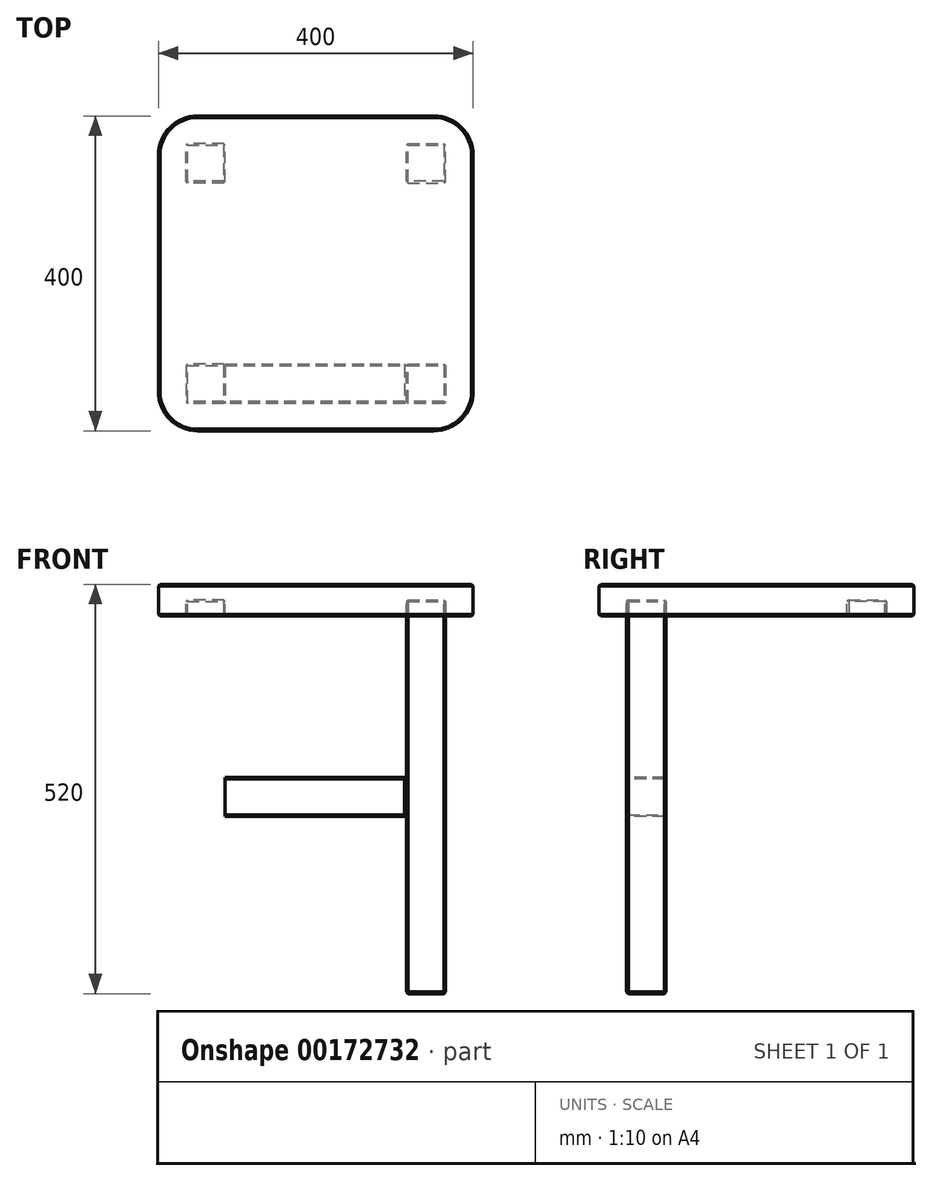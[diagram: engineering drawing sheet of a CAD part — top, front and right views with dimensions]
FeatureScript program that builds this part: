
annotation { "Feature Type Name" : "Feature", "Feature Type Description" : "" }
export const myFeature = defineFeature(function(context is Context, id is Id, definition is map)
    precondition{}
    {
        {
            var Q0;
            Q0=qCreatedBy(makeId("Top.planeOp"),FACE);
            var sketch = newSketch(context, id + "F0", { "sketchPlane" : qUnion([Q0])});
            skLineSegment(sketch, "E0.bottom", {"start": v(-200, -200) * mm, "end": v(200, -200) * mm});
            skLineSegment(sketch, "E0.top", {"start": v(-200, 200) * mm, "end": v(200, 200) * mm});
            skLineSegment(sketch, "E0.left", {"start": v(-200, -200) * mm, "end": v(-200, 200) * mm});
            skLineSegment(sketch, "E0.right", {"start": v(200, -200) * mm, "end": v(200, 200) * mm});
            skPoint(sketch, "E0.middle", {"position": v(0, 0) * mm});
            skSolve(sketch);
        }
        {
            var Q0;
            Q0=makeQuery(id+"F0.imprint","IMPRINT",FACE,{"disambiguationData":[TD([[makeQuery(id+"F0.imprint","IMPRINT",EDGE,{"derivedFrom":sQuery(id+"F0.wireOp",EDGE,"E0.bottom")}),1.0]])]});
            extrude(context, id + "F1", {"entities" : qUnion([Q0]), "depth" : 40 * mm});
        }
        {
            var Q0;
            Q0=makeQuery(id+"F1.opExtrude","CAP_FACE",FACE,{"disambiguationData":[OSD([sQuery(id+"F0.wireOp",EDGE,"E0.bottom"),sQuery(id+"F0.wireOp",EDGE,"E0.top"),sQuery(id+"F0.wireOp",EDGE,"E0.left"),sQuery(id+"F0.wireOp",EDGE,"E0.right")])],"isStart":true});
            var sketch = newSketch(context, id + "F2", { "sketchPlane" : qUnion([Q0])});
            skLineSegment(sketch, "E1.bottom", {"start": v(115, 115) * mm, "end": v(165, 115) * mm});
            skLineSegment(sketch, "E1.top", {"start": v(115, 165) * mm, "end": v(165, 165) * mm});
            skLineSegment(sketch, "E1.left", {"start": v(115, 115) * mm, "end": v(115, 165) * mm});
            skLineSegment(sketch, "E1.right", {"start": v(165, 115) * mm, "end": v(165, 165) * mm});
            skPoint(sketch, "E1.middle", {"position": v(140, 140) * mm});
            skLineSegment(sketch, "E2", {"start": v(140, 140) * mm, "end": v(200, 140) * mm, "construction": true});
            skLineSegment(sketch, "E3", {"start": v(140, 140) * mm, "end": v(140, 200) * mm, "construction": true});
            skLineSegment(sketch, "E4.MirrorCS", {"start": v(115, -115) * mm, "end": v(165, -115) * mm});
            skPoint(sketch, "E5.MirrorP", {"position": v(140, -140) * mm});
            skLineSegment(sketch, "E6.MirrorCS", {"start": v(165, -115) * mm, "end": v(165, -165) * mm});
            skLineSegment(sketch, "E7.MirrorCS", {"start": v(115, -165) * mm, "end": v(165, -165) * mm});
            skLineSegment(sketch, "E8.MirrorCS", {"start": v(115, -115) * mm, "end": v(115, -165) * mm});
            skPoint(sketch, "E9.MirrorP", {"position": v(-140, -140) * mm});
            skLineSegment(sketch, "E10.MirrorCS", {"start": v(-165, -115) * mm, "end": v(-165, -165) * mm});
            skLineSegment(sketch, "E11.MirrorCS", {"start": v(-115, -165) * mm, "end": v(-165, -165) * mm});
            skLineSegment(sketch, "E12.MirrorCS", {"start": v(-115, -115) * mm, "end": v(-165, -115) * mm});
            skLineSegment(sketch, "E13.MirrorCS", {"start": v(-115, -115) * mm, "end": v(-115, -165) * mm});
            skLineSegment(sketch, "E14.MirrorCS", {"start": v(-165, 115) * mm, "end": v(-165, 165) * mm});
            skLineSegment(sketch, "E15.MirrorCS", {"start": v(-115, 115) * mm, "end": v(-115, 165) * mm});
            skPoint(sketch, "E16.MirrorP", {"position": v(-140, 140) * mm});
            skLineSegment(sketch, "E17.MirrorCS", {"start": v(-115, 115) * mm, "end": v(-165, 115) * mm});
            skLineSegment(sketch, "E18.MirrorCS", {"start": v(-115, 165) * mm, "end": v(-165, 165) * mm});
            skSolve(sketch);
        }
        {
            var Q0;
            Q0 = qSketchRegion(id + "F2", true);
            extrude(context, id + "F3", {"entities" : qUnion([Q0]), "operationType" : NewBodyOperationType.REMOVE, "oppositeDirection" : true, "depth" : 20 * mm});
        }
        {
            var Q0;
            Q0=makeQuery(id+"F1.opExtrude","SWEPT_EDGE",EDGE,{"disambiguationData":[OSD([sQuery(id+"F0.wireOp",EDGE,"E0.bottom"),sQuery(id+"F0.wireOp",EDGE,"E0.right")])]});
            var Q1;
            Q1=makeQuery(id+"F1.opExtrude","SWEPT_EDGE",EDGE,{"disambiguationData":[OSD([sQuery(id+"F0.wireOp",EDGE,"E0.top"),sQuery(id+"F0.wireOp",EDGE,"E0.right")])]});
            var Q2;
            Q2=makeQuery(id+"F1.opExtrude","SWEPT_EDGE",EDGE,{"disambiguationData":[OSD([sQuery(id+"F0.wireOp",EDGE,"E0.top"),sQuery(id+"F0.wireOp",EDGE,"E0.left")])]});
            var Q3;
            Q3=makeQuery(id+"F1.opExtrude","SWEPT_EDGE",EDGE,{"disambiguationData":[OSD([sQuery(id+"F0.wireOp",EDGE,"E0.bottom"),sQuery(id+"F0.wireOp",EDGE,"E0.left")])]});
            fillet(context, id + "F4", {"entities" : qUnion([Q0, Q1, Q2, Q3]), "radius" : 50 * mm, "tangentPropagation" : true, "allowEdgeOverflow" : false});
        }
        {
            var Q0;
            Q0=makeQuery(id+"F3.boolean.opBoolean","COPY",FACE,{"derivedFrom":makeQuery(id+"F3.opExtrude","CAP_FACE",FACE,{"disambiguationData":[OSD([sQuery(id+"F2.wireOp",EDGE,"E1.bottom"),sQuery(id+"F2.wireOp",EDGE,"E1.top"),sQuery(id+"F2.wireOp",EDGE,"E1.left"),sQuery(id+"F2.wireOp",EDGE,"E1.right")])],"isStart":false})});
            extrude(context, id + "F5", {"entities" : qUnion([Q0]), "depth" : 500 * mm});
        }
        {
            var Q0;
            Q0=makeQuery(id+"F5.opExtrude","SWEPT_FACE",FACE,{"disambiguationData":[OSD([sQuery(id+"F2.wireOp",EDGE,"E1.left")])]});
            var sketch = newSketch(context, id + "F6", { "sketchPlane" : qUnion([Q0])});
            skLineSegment(sketch, "E19.bottom", {"start": v(165, -205) * mm, "end": v(115, -205) * mm});
            skLineSegment(sketch, "E19.top", {"start": v(165, -255) * mm, "end": v(115, -255) * mm});
            skLineSegment(sketch, "E19.left", {"start": v(165, -205) * mm, "end": v(165, -255) * mm});
            skLineSegment(sketch, "E19.right", {"start": v(115, -205) * mm, "end": v(115, -255) * mm});
            skSolve(sketch);
        }
        {
            var Q0;
            Q0 = qSketchRegion(id + "F6", true);
            var Q1;
            Q1=makeQuery(id+"F3.boolean.opBoolean","COPY",FACE,{"derivedFrom":makeQuery(id+"F3.opExtrude","SWEPT_FACE",FACE,{"disambiguationData":[OSD([sQuery(id+"F2.wireOp",EDGE,"E15.MirrorCS")])]})});
            extrude(context, id + "F7", {"entities" : qUnion([Q0]), "endBound" : BoundingType.UP_TO_SURFACE, "endBoundEntityFace" : qUnion([Q1]), "depth" : 25 * mm});
        }
        {
            var Q0;
            {var subQ0=sQuery(id+"F0.wireOp",EDGE,"E0.left");var subQ1=sQuery(id+"F0.wireOp",EDGE,"E0.bottom");Q0=makeQuery(id+"F4.opFillet","BLEND_EDGE",EDGE,{"blendedFrom":[makeQuery(id+"F1.opExtrude","SWEPT_EDGE",EDGE,{"disambiguationData":[OSD([subQ1,subQ0])]}),makeQuery(id+"F1.opExtrude","CAP_FACE",FACE,{"disambiguationData":[OSD([subQ1,sQuery(id+"F0.wireOp",EDGE,"E0.top"),subQ0,sQuery(id+"F0.wireOp",EDGE,"E0.right")])],"isStart":true})],"blendedInto":[makeQuery(id+"F1.opExtrude","CAP_FACE",FACE,{"disambiguationData":[OSD([subQ1,sQuery(id+"F0.wireOp",EDGE,"E0.top"),subQ0,sQuery(id+"F0.wireOp",EDGE,"E0.right")])],"isStart":true})]});}
            var Q1;
            {var subQ0=sQuery(id+"F0.wireOp",EDGE,"E0.right");var subQ1=sQuery(id+"F0.wireOp",EDGE,"E0.bottom");Q1=makeQuery(id+"F4.opFillet","BLEND_EDGE",EDGE,{"blendedFrom":[makeQuery(id+"F1.opExtrude","SWEPT_EDGE",EDGE,{"disambiguationData":[OSD([subQ1,subQ0])]}),makeQuery(id+"F1.opExtrude","CAP_FACE",FACE,{"disambiguationData":[OSD([subQ1,sQuery(id+"F0.wireOp",EDGE,"E0.top"),sQuery(id+"F0.wireOp",EDGE,"E0.left"),subQ0])],"isStart":false})],"blendedInto":[makeQuery(id+"F1.opExtrude","CAP_FACE",FACE,{"disambiguationData":[OSD([subQ1,sQuery(id+"F0.wireOp",EDGE,"E0.top"),sQuery(id+"F0.wireOp",EDGE,"E0.left"),subQ0])],"isStart":false})]});}
            var Q2;
            {var subQ0=sQuery(id+"F0.wireOp",EDGE,"E0.left");var subQ1=sQuery(id+"F0.wireOp",EDGE,"E0.top");Q2=makeQuery(id+"F4.opFillet","BLEND_EDGE",EDGE,{"blendedFrom":[makeQuery(id+"F1.opExtrude","SWEPT_EDGE",EDGE,{"disambiguationData":[OSD([subQ1,subQ0])]}),makeQuery(id+"F1.opExtrude","CAP_FACE",FACE,{"disambiguationData":[OSD([sQuery(id+"F0.wireOp",EDGE,"E0.bottom"),subQ1,subQ0,sQuery(id+"F0.wireOp",EDGE,"E0.right")])],"isStart":false})],"blendedInto":[makeQuery(id+"F1.opExtrude","CAP_FACE",FACE,{"disambiguationData":[OSD([sQuery(id+"F0.wireOp",EDGE,"E0.bottom"),subQ1,subQ0,sQuery(id+"F0.wireOp",EDGE,"E0.right")])],"isStart":false})]});}
            var Q3;
            {var subQ0=sQuery(id+"F0.wireOp",EDGE,"E0.left");var subQ1=sQuery(id+"F0.wireOp",EDGE,"E0.top");Q3=makeQuery(id+"F4.opFillet","BLEND_EDGE",EDGE,{"blendedFrom":[makeQuery(id+"F1.opExtrude","SWEPT_EDGE",EDGE,{"disambiguationData":[OSD([subQ1,subQ0])]}),makeQuery(id+"F1.opExtrude","CAP_FACE",FACE,{"disambiguationData":[OSD([sQuery(id+"F0.wireOp",EDGE,"E0.bottom"),subQ1,subQ0,sQuery(id+"F0.wireOp",EDGE,"E0.right")])],"isStart":true})],"blendedInto":[makeQuery(id+"F1.opExtrude","CAP_FACE",FACE,{"disambiguationData":[OSD([sQuery(id+"F0.wireOp",EDGE,"E0.bottom"),subQ1,subQ0,sQuery(id+"F0.wireOp",EDGE,"E0.right")])],"isStart":true})]});}
            var Q4;
            Q4=makeQuery(id+"F1.opExtrude","CAP_EDGE",EDGE,{"disambiguationData":[OSD([sQuery(id+"F0.wireOp",EDGE,"E0.bottom")])],"isStart":true});
            var Q5;
            Q5=makeQuery(id+"F1.opExtrude","CAP_EDGE",EDGE,{"disambiguationData":[OSD([sQuery(id+"F0.wireOp",EDGE,"E0.bottom")])],"isStart":false});
            var Q6;
            Q6=makeQuery(id+"F1.opExtrude","CAP_EDGE",EDGE,{"disambiguationData":[OSD([sQuery(id+"F0.wireOp",EDGE,"E0.left")])],"isStart":true});
            var Q7;
            Q7=makeQuery(id+"F1.opExtrude","CAP_EDGE",EDGE,{"disambiguationData":[OSD([sQuery(id+"F0.wireOp",EDGE,"E0.top")])],"isStart":false});
            var Q8;
            {var subQ0=sQuery(id+"F0.wireOp",EDGE,"E0.left");var subQ1=sQuery(id+"F0.wireOp",EDGE,"E0.bottom");Q8=makeQuery(id+"F4.opFillet","BLEND_EDGE",EDGE,{"blendedFrom":[makeQuery(id+"F1.opExtrude","SWEPT_EDGE",EDGE,{"disambiguationData":[OSD([subQ1,subQ0])]}),makeQuery(id+"F1.opExtrude","CAP_FACE",FACE,{"disambiguationData":[OSD([subQ1,sQuery(id+"F0.wireOp",EDGE,"E0.top"),subQ0,sQuery(id+"F0.wireOp",EDGE,"E0.right")])],"isStart":false})],"blendedInto":[makeQuery(id+"F1.opExtrude","CAP_FACE",FACE,{"disambiguationData":[OSD([subQ1,sQuery(id+"F0.wireOp",EDGE,"E0.top"),subQ0,sQuery(id+"F0.wireOp",EDGE,"E0.right")])],"isStart":false})]});}
            var Q9;
            Q9=makeQuery(id+"F1.opExtrude","CAP_EDGE",EDGE,{"disambiguationData":[OSD([sQuery(id+"F0.wireOp",EDGE,"E0.left")])],"isStart":false});
            var Q10;
            Q10=makeQuery(id+"F1.opExtrude","CAP_EDGE",EDGE,{"disambiguationData":[OSD([sQuery(id+"F0.wireOp",EDGE,"E0.right")])],"isStart":false});
            var Q11;
            {var subQ0=sQuery(id+"F0.wireOp",EDGE,"E0.right");var subQ1=sQuery(id+"F0.wireOp",EDGE,"E0.top");Q11=makeQuery(id+"F4.opFillet","BLEND_EDGE",EDGE,{"blendedFrom":[makeQuery(id+"F1.opExtrude","SWEPT_EDGE",EDGE,{"disambiguationData":[OSD([subQ1,subQ0])]}),makeQuery(id+"F1.opExtrude","CAP_FACE",FACE,{"disambiguationData":[OSD([sQuery(id+"F0.wireOp",EDGE,"E0.bottom"),subQ1,sQuery(id+"F0.wireOp",EDGE,"E0.left"),subQ0])],"isStart":false})],"blendedInto":[makeQuery(id+"F1.opExtrude","CAP_FACE",FACE,{"disambiguationData":[OSD([sQuery(id+"F0.wireOp",EDGE,"E0.bottom"),subQ1,sQuery(id+"F0.wireOp",EDGE,"E0.left"),subQ0])],"isStart":false})]});}
            var Q12;
            Q12=makeQuery(id+"F7.opExtrude","SWEPT_EDGE",EDGE,{"disambiguationData":[OSD([sQuery(id+"F2.wireOp",EDGE,"E1.top"),sQuery(id+"F2.wireOp",EDGE,"E1.left"),sQuery(id+"F6.wireOp",EDGE,"E19.bottom"),sQuery(id+"F6.wireOp",EDGE,"E19.left")])]});
            var Q13;
            Q13=makeQuery(id+"F7.opExtrude","SWEPT_EDGE",EDGE,{"disambiguationData":[OSD([sQuery(id+"F2.wireOp",EDGE,"E1.bottom"),sQuery(id+"F2.wireOp",EDGE,"E1.left"),sQuery(id+"F6.wireOp",EDGE,"E19.bottom"),sQuery(id+"F6.wireOp",EDGE,"E19.right")])]});
            var Q14;
            Q14=makeQuery(id+"F7.opExtrude","CAP_EDGE",EDGE,{"disambiguationData":[OSD([sQuery(id+"F6.wireOp",EDGE,"E19.bottom")])],"isStart":true});
            var Q15;
            Q15=makeQuery(id+"F7.opExtrude","SWEPT_EDGE",EDGE,{"disambiguationData":[OSD([sQuery(id+"F2.wireOp",EDGE,"E1.top"),sQuery(id+"F2.wireOp",EDGE,"E1.left"),sQuery(id+"F6.wireOp",EDGE,"E19.top"),sQuery(id+"F6.wireOp",EDGE,"E19.left")])]});
            var Q16;
            Q16=makeQuery(id+"F7.opExtrude","TWEAK_EDGE",EDGE,{"derivedFrom":[makeQuery(id+"F3.boolean.opBoolean","COPY",FACE,{"derivedFrom":makeQuery(id+"F3.opExtrude","SWEPT_FACE",FACE,{"disambiguationData":[OSD([sQuery(id+"F2.wireOp",EDGE,"E15.MirrorCS")])]})}),makeQuery(id+"F6.imprint","IMPRINT",EDGE,{"derivedFrom":sQuery(id+"F6.wireOp",EDGE,"E19.left")})]});
            var Q17;
            Q17=makeQuery(id+"F5.opExtrude","SWEPT_EDGE",EDGE,{"disambiguationData":[OSD([sQuery(id+"F2.wireOp",EDGE,"E1.top"),sQuery(id+"F2.wireOp",EDGE,"E1.left")])]});
            var Q18;
            Q18=makeQuery(id+"F5.opExtrude","SWEPT_EDGE",EDGE,{"disambiguationData":[OSD([sQuery(id+"F2.wireOp",EDGE,"E1.bottom"),sQuery(id+"F2.wireOp",EDGE,"E1.left")])]});
            var Q19;
            Q19=makeQuery(id+"F5.opExtrude","CAP_EDGE",EDGE,{"disambiguationData":[OSD([sQuery(id+"F2.wireOp",EDGE,"E1.left")])],"isStart":false});
            var Q20;
            Q20=makeQuery(id+"F5.opExtrude","SWEPT_EDGE",EDGE,{"disambiguationData":[OSD([sQuery(id+"F2.wireOp",EDGE,"E1.top"),sQuery(id+"F2.wireOp",EDGE,"E1.right")])]});
            var Q21;
            Q21=makeQuery(id+"F5.opExtrude","CAP_EDGE",EDGE,{"disambiguationData":[OSD([sQuery(id+"F2.wireOp",EDGE,"E1.top")])],"isStart":false});
            var Q22;
            {var subQ0=sQuery(id+"F0.wireOp",EDGE,"E0.bottom");Q22=makeQuery(id+"F4.opFillet","BLEND_EDGE",EDGE,{"blendedFrom":[makeQuery(id+"F1.opExtrude","SWEPT_EDGE",EDGE,{"disambiguationData":[OSD([subQ0,sQuery(id+"F0.wireOp",EDGE,"E0.right")])]}),makeQuery(id+"F1.opExtrude","SWEPT_FACE",FACE,{"disambiguationData":[OSD([subQ0])]})],"blendedInto":[makeQuery(id+"F1.opExtrude","SWEPT_FACE",FACE,{"disambiguationData":[OSD([subQ0])]})]});}
            var Q23;
            {var subQ0=sQuery(id+"F0.wireOp",EDGE,"E0.top");Q23=makeQuery(id+"F4.opFillet","BLEND_EDGE",EDGE,{"blendedFrom":[makeQuery(id+"F1.opExtrude","SWEPT_EDGE",EDGE,{"disambiguationData":[OSD([subQ0,sQuery(id+"F0.wireOp",EDGE,"E0.right")])]}),makeQuery(id+"F1.opExtrude","SWEPT_FACE",FACE,{"disambiguationData":[OSD([subQ0])]})],"blendedInto":[makeQuery(id+"F1.opExtrude","SWEPT_FACE",FACE,{"disambiguationData":[OSD([subQ0])]})]});}
            var Q24;
            {var subQ0=sQuery(id+"F0.wireOp",EDGE,"E0.right");var subQ1=sQuery(id+"F0.wireOp",EDGE,"E0.top");Q24=makeQuery(id+"F4.opFillet","BLEND_EDGE",EDGE,{"blendedFrom":[makeQuery(id+"F1.opExtrude","SWEPT_EDGE",EDGE,{"disambiguationData":[OSD([subQ1,subQ0])]}),makeQuery(id+"F1.opExtrude","CAP_FACE",FACE,{"disambiguationData":[OSD([sQuery(id+"F0.wireOp",EDGE,"E0.bottom"),subQ1,sQuery(id+"F0.wireOp",EDGE,"E0.left"),subQ0])],"isStart":true})],"blendedInto":[makeQuery(id+"F1.opExtrude","CAP_FACE",FACE,{"disambiguationData":[OSD([sQuery(id+"F0.wireOp",EDGE,"E0.bottom"),subQ1,sQuery(id+"F0.wireOp",EDGE,"E0.left"),subQ0])],"isStart":true})]});}
            var Q25;
            {var subQ0=sQuery(id+"F0.wireOp",EDGE,"E0.left");Q25=makeQuery(id+"F4.opFillet","BLEND_EDGE",EDGE,{"blendedFrom":[makeQuery(id+"F1.opExtrude","SWEPT_EDGE",EDGE,{"disambiguationData":[OSD([sQuery(id+"F0.wireOp",EDGE,"E0.bottom"),subQ0])]}),makeQuery(id+"F1.opExtrude","SWEPT_FACE",FACE,{"disambiguationData":[OSD([subQ0])]})],"blendedInto":[makeQuery(id+"F1.opExtrude","SWEPT_FACE",FACE,{"disambiguationData":[OSD([subQ0])]})]});}
            var Q26;
            Q26=makeQuery(id+"F3.boolean.opBoolean","COPY",EDGE,{"derivedFrom":makeQuery(id+"F3.opExtrude","CAP_EDGE",EDGE,{"disambiguationData":[OSD([sQuery(id+"F2.wireOp",EDGE,"E18.MirrorCS")])],"isStart":true})});
            var Q27;
            {var subQ0=sQuery(id+"F0.wireOp",EDGE,"E0.right");Q27=makeQuery(id+"F4.opFillet","BLEND_EDGE",EDGE,{"blendedFrom":[makeQuery(id+"F1.opExtrude","SWEPT_EDGE",EDGE,{"disambiguationData":[OSD([sQuery(id+"F0.wireOp",EDGE,"E0.top"),subQ0])]}),makeQuery(id+"F1.opExtrude","SWEPT_FACE",FACE,{"disambiguationData":[OSD([subQ0])]})],"blendedInto":[makeQuery(id+"F1.opExtrude","SWEPT_FACE",FACE,{"disambiguationData":[OSD([subQ0])]})]});}
            var Q28;
            Q28=makeQuery(id+"F3.boolean.opBoolean","COPY",EDGE,{"derivedFrom":makeQuery(id+"F3.opExtrude","CAP_EDGE",EDGE,{"disambiguationData":[OSD([sQuery(id+"F2.wireOp",EDGE,"E7.MirrorCS")])],"isStart":false})});
            var Q29;
            {var subQ0=sQuery(id+"F0.wireOp",EDGE,"E0.right");Q29=makeQuery(id+"F4.opFillet","BLEND_EDGE",EDGE,{"blendedFrom":[makeQuery(id+"F1.opExtrude","SWEPT_EDGE",EDGE,{"disambiguationData":[OSD([sQuery(id+"F0.wireOp",EDGE,"E0.bottom"),subQ0])]}),makeQuery(id+"F1.opExtrude","SWEPT_FACE",FACE,{"disambiguationData":[OSD([subQ0])]})],"blendedInto":[makeQuery(id+"F1.opExtrude","SWEPT_FACE",FACE,{"disambiguationData":[OSD([subQ0])]})]});}
            var Q30;
            {var subQ0=sQuery(id+"F0.wireOp",EDGE,"E0.left");Q30=makeQuery(id+"F4.opFillet","BLEND_EDGE",EDGE,{"blendedFrom":[makeQuery(id+"F1.opExtrude","SWEPT_EDGE",EDGE,{"disambiguationData":[OSD([sQuery(id+"F0.wireOp",EDGE,"E0.top"),subQ0])]}),makeQuery(id+"F1.opExtrude","SWEPT_FACE",FACE,{"disambiguationData":[OSD([subQ0])]})],"blendedInto":[makeQuery(id+"F1.opExtrude","SWEPT_FACE",FACE,{"disambiguationData":[OSD([subQ0])]})]});}
            var Q31;
            Q31=makeQuery(id+"F1.opExtrude","CAP_EDGE",EDGE,{"disambiguationData":[OSD([sQuery(id+"F0.wireOp",EDGE,"E0.right")])],"isStart":true});
            var Q32;
            Q32=makeQuery(id+"F3.boolean.opBoolean","COPY",EDGE,{"derivedFrom":makeQuery(id+"F3.opExtrude","CAP_EDGE",EDGE,{"disambiguationData":[OSD([sQuery(id+"F2.wireOp",EDGE,"E1.left")])],"isStart":true})});
            var Q33;
            Q33=makeQuery(id+"F1.opExtrude","CAP_EDGE",EDGE,{"disambiguationData":[OSD([sQuery(id+"F0.wireOp",EDGE,"E0.top")])],"isStart":true});
            var Q34;
            {var subQ0=sQuery(id+"F0.wireOp",EDGE,"E0.top");Q34=makeQuery(id+"F4.opFillet","BLEND_EDGE",EDGE,{"blendedFrom":[makeQuery(id+"F1.opExtrude","SWEPT_EDGE",EDGE,{"disambiguationData":[OSD([subQ0,sQuery(id+"F0.wireOp",EDGE,"E0.left")])]}),makeQuery(id+"F1.opExtrude","SWEPT_FACE",FACE,{"disambiguationData":[OSD([subQ0])]})],"blendedInto":[makeQuery(id+"F1.opExtrude","SWEPT_FACE",FACE,{"disambiguationData":[OSD([subQ0])]})]});}
            var Q35;
            Q35=makeQuery(id+"F3.boolean.opBoolean","COPY",EDGE,{"derivedFrom":makeQuery(id+"F3.opExtrude","CAP_EDGE",EDGE,{"disambiguationData":[OSD([sQuery(id+"F2.wireOp",EDGE,"E12.MirrorCS")])],"isStart":false})});
            var Q36;
            Q36=makeQuery(id+"F3.boolean.opBoolean","COPY",EDGE,{"derivedFrom":makeQuery(id+"F3.opExtrude","CAP_EDGE",EDGE,{"disambiguationData":[OSD([sQuery(id+"F2.wireOp",EDGE,"E1.bottom")])],"isStart":false})});
            var Q37;
            {var subQ0=sQuery(id+"F0.wireOp",EDGE,"E0.bottom");Q37=makeQuery(id+"F4.opFillet","BLEND_EDGE",EDGE,{"blendedFrom":[makeQuery(id+"F1.opExtrude","SWEPT_EDGE",EDGE,{"disambiguationData":[OSD([subQ0,sQuery(id+"F0.wireOp",EDGE,"E0.left")])]}),makeQuery(id+"F1.opExtrude","SWEPT_FACE",FACE,{"disambiguationData":[OSD([subQ0])]})],"blendedInto":[makeQuery(id+"F1.opExtrude","SWEPT_FACE",FACE,{"disambiguationData":[OSD([subQ0])]})]});}
            var Q38;
            {var subQ0=sQuery(id+"F0.wireOp",EDGE,"E0.right");var subQ1=sQuery(id+"F0.wireOp",EDGE,"E0.bottom");Q38=makeQuery(id+"F4.opFillet","BLEND_EDGE",EDGE,{"blendedFrom":[makeQuery(id+"F1.opExtrude","SWEPT_EDGE",EDGE,{"disambiguationData":[OSD([subQ1,subQ0])]}),makeQuery(id+"F1.opExtrude","CAP_FACE",FACE,{"disambiguationData":[OSD([subQ1,sQuery(id+"F0.wireOp",EDGE,"E0.top"),sQuery(id+"F0.wireOp",EDGE,"E0.left"),subQ0])],"isStart":true})],"blendedInto":[makeQuery(id+"F1.opExtrude","CAP_FACE",FACE,{"disambiguationData":[OSD([subQ1,sQuery(id+"F0.wireOp",EDGE,"E0.top"),sQuery(id+"F0.wireOp",EDGE,"E0.left"),subQ0])],"isStart":true})]});}
            var Q39;
            Q39=makeQuery(id+"F7.opExtrude","TWEAK_EDGE",EDGE,{"derivedFrom":[makeQuery(id+"F3.boolean.opBoolean","COPY",FACE,{"derivedFrom":makeQuery(id+"F3.opExtrude","SWEPT_FACE",FACE,{"disambiguationData":[OSD([sQuery(id+"F2.wireOp",EDGE,"E15.MirrorCS")])]})}),makeQuery(id+"F6.imprint","IMPRINT",EDGE,{"derivedFrom":sQuery(id+"F6.wireOp",EDGE,"E19.top")})]});
            var Q40;
            Q40=makeQuery(id+"F7.opExtrude","TWEAK_EDGE",EDGE,{"derivedFrom":[makeQuery(id+"F3.boolean.opBoolean","COPY",FACE,{"derivedFrom":makeQuery(id+"F3.opExtrude","SWEPT_FACE",FACE,{"disambiguationData":[OSD([sQuery(id+"F2.wireOp",EDGE,"E15.MirrorCS")])]})}),makeQuery(id+"F6.imprint","IMPRINT",EDGE,{"derivedFrom":sQuery(id+"F6.wireOp",EDGE,"E19.right")})]});
            var Q41;
            Q41=makeQuery(id+"F7.opExtrude","CAP_EDGE",EDGE,{"disambiguationData":[OSD([sQuery(id+"F6.wireOp",EDGE,"E19.top")])],"isStart":true});
            var Q42;
            Q42=makeQuery(id+"F7.opExtrude","CAP_EDGE",EDGE,{"disambiguationData":[OSD([sQuery(id+"F6.wireOp",EDGE,"E19.left")])],"isStart":true});
            var Q43;
            Q43=makeQuery(id+"F7.opExtrude","CAP_EDGE",EDGE,{"disambiguationData":[OSD([sQuery(id+"F6.wireOp",EDGE,"E19.right")])],"isStart":true});
            var Q44;
            Q44=makeQuery(id+"F7.opExtrude","TWEAK_EDGE",EDGE,{"derivedFrom":[makeQuery(id+"F3.boolean.opBoolean","COPY",FACE,{"derivedFrom":makeQuery(id+"F3.opExtrude","SWEPT_FACE",FACE,{"disambiguationData":[OSD([sQuery(id+"F2.wireOp",EDGE,"E15.MirrorCS")])]})}),makeQuery(id+"F6.imprint","IMPRINT",EDGE,{"derivedFrom":sQuery(id+"F6.wireOp",EDGE,"E19.bottom")})]});
            var Q45;
            Q45=makeQuery(id+"F7.opExtrude","SWEPT_EDGE",EDGE,{"disambiguationData":[OSD([sQuery(id+"F2.wireOp",EDGE,"E1.bottom"),sQuery(id+"F2.wireOp",EDGE,"E1.left"),sQuery(id+"F6.wireOp",EDGE,"E19.top"),sQuery(id+"F6.wireOp",EDGE,"E19.right")])]});
            var Q46;
            Q46=makeQuery(id+"F5.opExtrude","CAP_EDGE",EDGE,{"disambiguationData":[OSD([sQuery(id+"F2.wireOp",EDGE,"E1.bottom")])],"isStart":false});
            var Q47;
            Q47=makeQuery(id+"F5.opExtrude","SWEPT_EDGE",EDGE,{"disambiguationData":[OSD([sQuery(id+"F2.wireOp",EDGE,"E1.bottom"),sQuery(id+"F2.wireOp",EDGE,"E1.right")])]});
            var Q48;
            Q48=makeQuery(id+"F5.opExtrude","CAP_EDGE",EDGE,{"disambiguationData":[OSD([sQuery(id+"F2.wireOp",EDGE,"E1.right")])],"isStart":false});
            var Q49;
            Q49=makeQuery(id+"F3.boolean.opBoolean","COPY",EDGE,{"derivedFrom":makeQuery(id+"F3.opExtrude","CAP_EDGE",EDGE,{"disambiguationData":[OSD([sQuery(id+"F2.wireOp",EDGE,"E4.MirrorCS")])],"isStart":true})});
            var Q50;
            Q50=makeQuery(id+"F3.boolean.opBoolean","COPY",EDGE,{"derivedFrom":makeQuery(id+"F3.opExtrude","CAP_EDGE",EDGE,{"disambiguationData":[OSD([sQuery(id+"F2.wireOp",EDGE,"E15.MirrorCS")])],"isStart":true})});
            var Q51;
            Q51=makeQuery(id+"F3.boolean.opBoolean","COPY",EDGE,{"derivedFrom":makeQuery(id+"F3.opExtrude","CAP_EDGE",EDGE,{"disambiguationData":[OSD([sQuery(id+"F2.wireOp",EDGE,"E7.MirrorCS")])],"isStart":true})});
            var Q52;
            Q52=makeQuery(id+"F3.boolean.opBoolean","COPY",EDGE,{"derivedFrom":makeQuery(id+"F3.opExtrude","CAP_EDGE",EDGE,{"disambiguationData":[OSD([sQuery(id+"F2.wireOp",EDGE,"E1.right")])],"isStart":false})});
            var Q53;
            Q53=makeQuery(id+"F3.boolean.opBoolean","COPY",EDGE,{"derivedFrom":makeQuery(id+"F3.opExtrude","CAP_EDGE",EDGE,{"disambiguationData":[OSD([sQuery(id+"F2.wireOp",EDGE,"E13.MirrorCS")])],"isStart":false})});
            var Q54;
            Q54=makeQuery(id+"F3.boolean.opBoolean","COPY",EDGE,{"derivedFrom":makeQuery(id+"F3.opExtrude","CAP_EDGE",EDGE,{"disambiguationData":[OSD([sQuery(id+"F2.wireOp",EDGE,"E6.MirrorCS")])],"isStart":true})});
            var Q55;
            Q55=makeQuery(id+"F3.boolean.opBoolean","COPY",EDGE,{"derivedFrom":makeQuery(id+"F3.opExtrude","CAP_EDGE",EDGE,{"disambiguationData":[OSD([sQuery(id+"F2.wireOp",EDGE,"E11.MirrorCS")])],"isStart":true})});
            var Q56;
            Q56=makeQuery(id+"F3.boolean.opBoolean","COPY",EDGE,{"derivedFrom":makeQuery(id+"F3.opExtrude","SWEPT_EDGE",EDGE,{"disambiguationData":[OSD([sQuery(id+"F2.wireOp",EDGE,"E7.MirrorCS"),sQuery(id+"F2.wireOp",EDGE,"E6.MirrorCS")])]})});
            var Q57;
            Q57=makeQuery(id+"F3.boolean.opBoolean","COPY",EDGE,{"derivedFrom":makeQuery(id+"F3.opExtrude","CAP_EDGE",EDGE,{"disambiguationData":[OSD([sQuery(id+"F2.wireOp",EDGE,"E1.top")])],"isStart":false})});
            var Q58;
            Q58=makeQuery(id+"F3.boolean.opBoolean","COPY",EDGE,{"derivedFrom":makeQuery(id+"F3.opExtrude","CAP_EDGE",EDGE,{"disambiguationData":[OSD([sQuery(id+"F2.wireOp",EDGE,"E14.MirrorCS")])],"isStart":false})});
            var Q59;
            Q59=makeQuery(id+"F3.boolean.opBoolean","COPY",EDGE,{"derivedFrom":makeQuery(id+"F3.opExtrude","CAP_EDGE",EDGE,{"disambiguationData":[OSD([sQuery(id+"F2.wireOp",EDGE,"E14.MirrorCS")])],"isStart":true})});
            var Q60;
            Q60=makeQuery(id+"F3.boolean.opBoolean","COPY",EDGE,{"derivedFrom":makeQuery(id+"F3.opExtrude","CAP_EDGE",EDGE,{"disambiguationData":[OSD([sQuery(id+"F2.wireOp",EDGE,"E10.MirrorCS")])],"isStart":true})});
            var Q61;
            Q61=makeQuery(id+"F3.boolean.opBoolean","COPY",EDGE,{"derivedFrom":makeQuery(id+"F3.opExtrude","CAP_EDGE",EDGE,{"disambiguationData":[OSD([sQuery(id+"F2.wireOp",EDGE,"E11.MirrorCS")])],"isStart":false})});
            var Q62;
            Q62=makeQuery(id+"F3.boolean.opBoolean","COPY",EDGE,{"derivedFrom":makeQuery(id+"F3.opExtrude","CAP_EDGE",EDGE,{"disambiguationData":[OSD([sQuery(id+"F2.wireOp",EDGE,"E10.MirrorCS")])],"isStart":false})});
            var Q63;
            Q63=makeQuery(id+"F3.boolean.opBoolean","COPY",EDGE,{"derivedFrom":makeQuery(id+"F3.opExtrude","CAP_EDGE",EDGE,{"disambiguationData":[OSD([sQuery(id+"F2.wireOp",EDGE,"E4.MirrorCS")])],"isStart":false})});
            var Q64;
            Q64=makeQuery(id+"F3.boolean.opBoolean","COPY",EDGE,{"derivedFrom":makeQuery(id+"F3.opExtrude","CAP_EDGE",EDGE,{"disambiguationData":[OSD([sQuery(id+"F2.wireOp",EDGE,"E13.MirrorCS")])],"isStart":true})});
            var Q65;
            Q65=makeQuery(id+"F3.boolean.opBoolean","COPY",EDGE,{"derivedFrom":makeQuery(id+"F3.opExtrude","CAP_EDGE",EDGE,{"disambiguationData":[OSD([sQuery(id+"F2.wireOp",EDGE,"E18.MirrorCS")])],"isStart":false})});
            var Q66;
            Q66=makeQuery(id+"F3.boolean.opBoolean","COPY",EDGE,{"derivedFrom":makeQuery(id+"F3.opExtrude","SWEPT_EDGE",EDGE,{"disambiguationData":[OSD([sQuery(id+"F2.wireOp",EDGE,"E14.MirrorCS"),sQuery(id+"F2.wireOp",EDGE,"E18.MirrorCS")])]})});
            var Q67;
            Q67=makeQuery(id+"F3.boolean.opBoolean","COPY",EDGE,{"derivedFrom":makeQuery(id+"F3.opExtrude","CAP_EDGE",EDGE,{"disambiguationData":[OSD([sQuery(id+"F2.wireOp",EDGE,"E1.left")])],"isStart":false})});
            var Q68;
            Q68=makeQuery(id+"F3.boolean.opBoolean","COPY",EDGE,{"derivedFrom":makeQuery(id+"F3.opExtrude","SWEPT_EDGE",EDGE,{"disambiguationData":[OSD([sQuery(id+"F2.wireOp",EDGE,"E8.MirrorCS"),sQuery(id+"F2.wireOp",EDGE,"E4.MirrorCS")])]})});
            var Q69;
            Q69=makeQuery(id+"F3.boolean.opBoolean","COPY",EDGE,{"derivedFrom":makeQuery(id+"F3.opExtrude","SWEPT_EDGE",EDGE,{"disambiguationData":[OSD([sQuery(id+"F2.wireOp",EDGE,"E10.MirrorCS"),sQuery(id+"F2.wireOp",EDGE,"E12.MirrorCS")])]})});
            var Q70;
            Q70=makeQuery(id+"F3.boolean.opBoolean","COPY",EDGE,{"derivedFrom":makeQuery(id+"F3.opExtrude","SWEPT_EDGE",EDGE,{"disambiguationData":[OSD([sQuery(id+"F2.wireOp",EDGE,"E14.MirrorCS"),sQuery(id+"F2.wireOp",EDGE,"E17.MirrorCS")])]})});
            var Q71;
            Q71=makeQuery(id+"F3.boolean.opBoolean","COPY",EDGE,{"derivedFrom":makeQuery(id+"F3.opExtrude","CAP_EDGE",EDGE,{"disambiguationData":[OSD([sQuery(id+"F2.wireOp",EDGE,"E6.MirrorCS")])],"isStart":false})});
            var Q72;
            Q72=makeQuery(id+"F3.boolean.opBoolean","COPY",EDGE,{"derivedFrom":makeQuery(id+"F3.opExtrude","SWEPT_EDGE",EDGE,{"disambiguationData":[OSD([sQuery(id+"F2.wireOp",EDGE,"E15.MirrorCS"),sQuery(id+"F2.wireOp",EDGE,"E18.MirrorCS")])]})});
            var Q73;
            Q73=makeQuery(id+"F3.boolean.opBoolean","COPY",EDGE,{"derivedFrom":makeQuery(id+"F3.opExtrude","CAP_EDGE",EDGE,{"disambiguationData":[OSD([sQuery(id+"F2.wireOp",EDGE,"E1.top")])],"isStart":true})});
            var Q74;
            Q74=makeQuery(id+"F3.boolean.opBoolean","COPY",EDGE,{"derivedFrom":makeQuery(id+"F3.opExtrude","SWEPT_EDGE",EDGE,{"disambiguationData":[OSD([sQuery(id+"F2.wireOp",EDGE,"E10.MirrorCS"),sQuery(id+"F2.wireOp",EDGE,"E11.MirrorCS")])]})});
            var Q75;
            Q75=makeQuery(id+"F3.boolean.opBoolean","COPY",EDGE,{"derivedFrom":makeQuery(id+"F3.opExtrude","CAP_EDGE",EDGE,{"disambiguationData":[OSD([sQuery(id+"F2.wireOp",EDGE,"E17.MirrorCS")])],"isStart":true})});
            var Q76;
            Q76=makeQuery(id+"F3.boolean.opBoolean","COPY",EDGE,{"derivedFrom":makeQuery(id+"F3.opExtrude","CAP_EDGE",EDGE,{"disambiguationData":[OSD([sQuery(id+"F2.wireOp",EDGE,"E8.MirrorCS")])],"isStart":false})});
            var Q77;
            Q77=makeQuery(id+"F3.boolean.opBoolean","COPY",EDGE,{"derivedFrom":makeQuery(id+"F3.opExtrude","CAP_EDGE",EDGE,{"disambiguationData":[OSD([sQuery(id+"F2.wireOp",EDGE,"E1.right")])],"isStart":true})});
            var Q78;
            Q78=makeQuery(id+"F3.boolean.opBoolean","COPY",EDGE,{"derivedFrom":makeQuery(id+"F3.opExtrude","SWEPT_EDGE",EDGE,{"disambiguationData":[OSD([sQuery(id+"F2.wireOp",EDGE,"E15.MirrorCS"),sQuery(id+"F2.wireOp",EDGE,"E17.MirrorCS")])]})});
            var Q79;
            Q79=makeQuery(id+"F3.boolean.opBoolean","COPY",EDGE,{"derivedFrom":makeQuery(id+"F3.opExtrude","CAP_EDGE",EDGE,{"disambiguationData":[OSD([sQuery(id+"F2.wireOp",EDGE,"E8.MirrorCS")])],"isStart":true})});
            var Q80;
            Q80=makeQuery(id+"F3.boolean.opBoolean","COPY",EDGE,{"derivedFrom":makeQuery(id+"F3.opExtrude","SWEPT_EDGE",EDGE,{"disambiguationData":[OSD([sQuery(id+"F2.wireOp",EDGE,"E13.MirrorCS"),sQuery(id+"F2.wireOp",EDGE,"E12.MirrorCS")])]})});
            var Q81;
            Q81=makeQuery(id+"F3.boolean.opBoolean","COPY",EDGE,{"derivedFrom":makeQuery(id+"F3.opExtrude","CAP_EDGE",EDGE,{"disambiguationData":[OSD([sQuery(id+"F2.wireOp",EDGE,"E12.MirrorCS")])],"isStart":true})});
            var Q82;
            Q82=makeQuery(id+"F3.boolean.opBoolean","COPY",EDGE,{"derivedFrom":makeQuery(id+"F3.opExtrude","SWEPT_EDGE",EDGE,{"disambiguationData":[OSD([sQuery(id+"F2.wireOp",EDGE,"E7.MirrorCS"),sQuery(id+"F2.wireOp",EDGE,"E8.MirrorCS")])]})});
            var Q83;
            Q83=makeQuery(id+"F3.boolean.opBoolean","COPY",EDGE,{"derivedFrom":makeQuery(id+"F3.opExtrude","CAP_EDGE",EDGE,{"disambiguationData":[OSD([sQuery(id+"F2.wireOp",EDGE,"E15.MirrorCS")])],"isStart":false})});
            var Q84;
            Q84=makeQuery(id+"F3.boolean.opBoolean","COPY",EDGE,{"derivedFrom":makeQuery(id+"F3.opExtrude","CAP_EDGE",EDGE,{"disambiguationData":[OSD([sQuery(id+"F2.wireOp",EDGE,"E17.MirrorCS")])],"isStart":false})});
            var Q85;
            Q85=makeQuery(id+"F3.boolean.opBoolean","COPY",EDGE,{"derivedFrom":makeQuery(id+"F3.opExtrude","CAP_EDGE",EDGE,{"disambiguationData":[OSD([sQuery(id+"F2.wireOp",EDGE,"E1.bottom")])],"isStart":true})});
            var Q86;
            Q86=makeQuery(id+"F3.boolean.opBoolean","COPY",EDGE,{"derivedFrom":makeQuery(id+"F3.opExtrude","SWEPT_EDGE",EDGE,{"disambiguationData":[OSD([sQuery(id+"F2.wireOp",EDGE,"E4.MirrorCS"),sQuery(id+"F2.wireOp",EDGE,"E6.MirrorCS")])]})});
            var Q87;
            Q87=makeQuery(id+"F3.boolean.opBoolean","COPY",EDGE,{"derivedFrom":makeQuery(id+"F3.opExtrude","SWEPT_EDGE",EDGE,{"disambiguationData":[OSD([sQuery(id+"F2.wireOp",EDGE,"E13.MirrorCS"),sQuery(id+"F2.wireOp",EDGE,"E11.MirrorCS")])]})});
            var Q88;
            Q88=makeQuery(id+"F5.opExtrude","CAP_EDGE",EDGE,{"disambiguationData":[OSD([sQuery(id+"F2.wireOp",EDGE,"E1.bottom")])],"isStart":true});
            var Q89;
            Q89=makeQuery(id+"F3.boolean.opBoolean","COPY",EDGE,{"derivedFrom":makeQuery(id+"F3.opExtrude","SWEPT_EDGE",EDGE,{"disambiguationData":[OSD([sQuery(id+"F2.wireOp",EDGE,"E1.top"),sQuery(id+"F2.wireOp",EDGE,"E1.right")])]})});
            var Q90;
            Q90=makeQuery(id+"F3.boolean.opBoolean","COPY",EDGE,{"derivedFrom":makeQuery(id+"F3.opExtrude","SWEPT_EDGE",EDGE,{"disambiguationData":[OSD([sQuery(id+"F2.wireOp",EDGE,"E1.bottom"),sQuery(id+"F2.wireOp",EDGE,"E1.right")])]})});
            var Q91;
            Q91=makeQuery(id+"F3.boolean.opBoolean","COPY",EDGE,{"derivedFrom":makeQuery(id+"F3.opExtrude","SWEPT_EDGE",EDGE,{"disambiguationData":[OSD([sQuery(id+"F2.wireOp",EDGE,"E1.bottom"),sQuery(id+"F2.wireOp",EDGE,"E1.left")])]})});
            var Q92;
            Q92=makeQuery(id+"F3.boolean.opBoolean","COPY",EDGE,{"derivedFrom":makeQuery(id+"F3.opExtrude","SWEPT_EDGE",EDGE,{"disambiguationData":[OSD([sQuery(id+"F2.wireOp",EDGE,"E1.top"),sQuery(id+"F2.wireOp",EDGE,"E1.left")])]})});
            var Q93;
            Q93=makeQuery(id+"F5.opExtrude","CAP_EDGE",EDGE,{"disambiguationData":[OSD([sQuery(id+"F2.wireOp",EDGE,"E1.right")])],"isStart":true});
            var Q94;
            Q94=makeQuery(id+"F5.opExtrude","CAP_EDGE",EDGE,{"disambiguationData":[OSD([sQuery(id+"F2.wireOp",EDGE,"E1.top")])],"isStart":true});
            var Q95;
            Q95=makeQuery(id+"F5.opExtrude","CAP_EDGE",EDGE,{"disambiguationData":[OSD([sQuery(id+"F2.wireOp",EDGE,"E1.left")])],"isStart":true});
            chamfer(context, id + "F8", {"entities" : qUnion([Q0, Q1, Q2, Q3, Q4, Q5, Q6, Q7, Q8, Q9, Q10, Q11, Q12, Q13, Q14, Q15, Q16, Q17, Q18, Q19, Q20, Q21, Q22, Q23, Q24, Q25, Q26, Q27, Q28, Q29, Q30, Q31, Q32, Q33, Q34, Q35, Q36, Q37, Q38, Q39, Q40, Q41, Q42, Q43, Q44, Q45, Q46, Q47, Q48, Q49, Q50, Q51, Q52, Q53, Q54, Q55, Q56, Q57, Q58, Q59, Q60, Q61, Q62, Q63, Q64, Q65, Q66, Q67, Q68, Q69, Q70, Q71, Q72, Q73, Q74, Q75, Q76, Q77, Q78, Q79, Q80, Q81, Q82, Q83, Q84, Q85, Q86, Q87, Q88, Q89, Q90, Q91, Q92, Q93, Q94, Q95]), "width" : 2 * mm, "tangentPropagation" : true});
        }
    });
